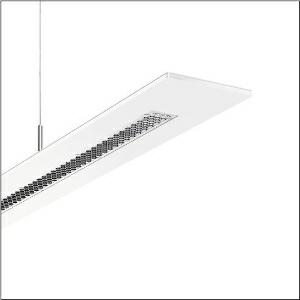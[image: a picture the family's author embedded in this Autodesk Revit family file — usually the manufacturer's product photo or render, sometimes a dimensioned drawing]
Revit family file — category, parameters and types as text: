
# Revit family: arktika_r__21_duo_5mb252dl60830_d82e
name_source: partatom
category: Lighting Fixtures
units: mm (PartAtom-declared; Revit-internal decimal feet)

## family parameters
Cut with Voids When Loaded = No
Host = Face
Light Source = No
Part Type = Normal
Room Calculation Point = No
Round Connector Dimension = Use Diameter
Shared = No

## types (1)
- --- (1 x LED 3000K / CRI = 80 (unbekannt), 8100 lm, 3000K)
    Apparent Load = 67 VA
    CIE Flux Codes = 81 100 100 79 100
    Color Rendering = 80
    Color Temperature = 3000K
    Default Elevation = 1800 mm
    Description = Arktika® 21 duo, office luminaire, primary anti-glare with honeycomb louvre, of plastic, aluminium vaporised, highly specular, light emission: direct/indirect distribution, primary light characteristic: symmetric, installation type: suspended mounting, LED, rated luminous flux: 8.100lm, luminous efficacy: 122lm/W, light colour: 830, colour temperature: 3000K, control gear: DALI, with terminal, 3+2-pole, max. 2.5mm², mains connection: 220..240V, AC, 50/60Hz, rated input power: 67W, housing, of aluminium, powder-coated, traffic white (RAL 9016), 2-length, length: 2.280mm, width: 120mm, height: 8mm, protection rating (complete): IP20, insulation class (complete): insulation class II (safety insulation), certification: CE, packaging unit: 1 piece
    Height = 8 mm  [stored 0.0262467 ft]
    Lamp = 1 x LED 3000K / CRI >= 80 (unbekannt)
    Lamp Light Flux = 8100 lm
    Lamp count = 1
    Length = 2280 mm
    Luminous efficacy = 122 lm/W
    Manufacturer = Siteco
    ModVariant = No
    Model = 5MB252DL60830
    Mounting Place = Ceiling
    Mounting Type = Pendant
    Number of Poles = 1
    OnlyDefault = Yes
    Power Factor = 1
    Product Name = Arktika® 21 duo
    Product group = office luminaire | ceiling pendant
    ProductGroupID = 903
    Protection Class = Protection class II
    Protection Degree = IP 20
    RLX_Detail_Level = 1
    RLX_Emergency_Light_Flux = 0 lm
    RLX_Emergency_Type = 0
    RLX_Emergency_Type_DB = No
    RlxData = <blob elided: 39765 chars, md5=a66dfcba>
    Socket = socket
    Standby Power = 0 W
    System Light Flux = 8100 lm
    System Power = 67 W
    Type Comments = factory setting: luminous flux: 100 % | dim-lin: 254 | 1330 mA
    Type Image = l_1006128.jpg
    URL = http://relux.com
    VarID = @adj_219865
    Voltage = 0 V
    Weight = 0.00 kg
    Width = 120 mm

note: [stored X ft] marks values corroborated as IEEE doubles in the binary element streams (Revit-internal decimal feet)

## geometry (parser evidence)
native form markers: Blend x4, Sweep x11
no freeform markers — native parametric forms only
